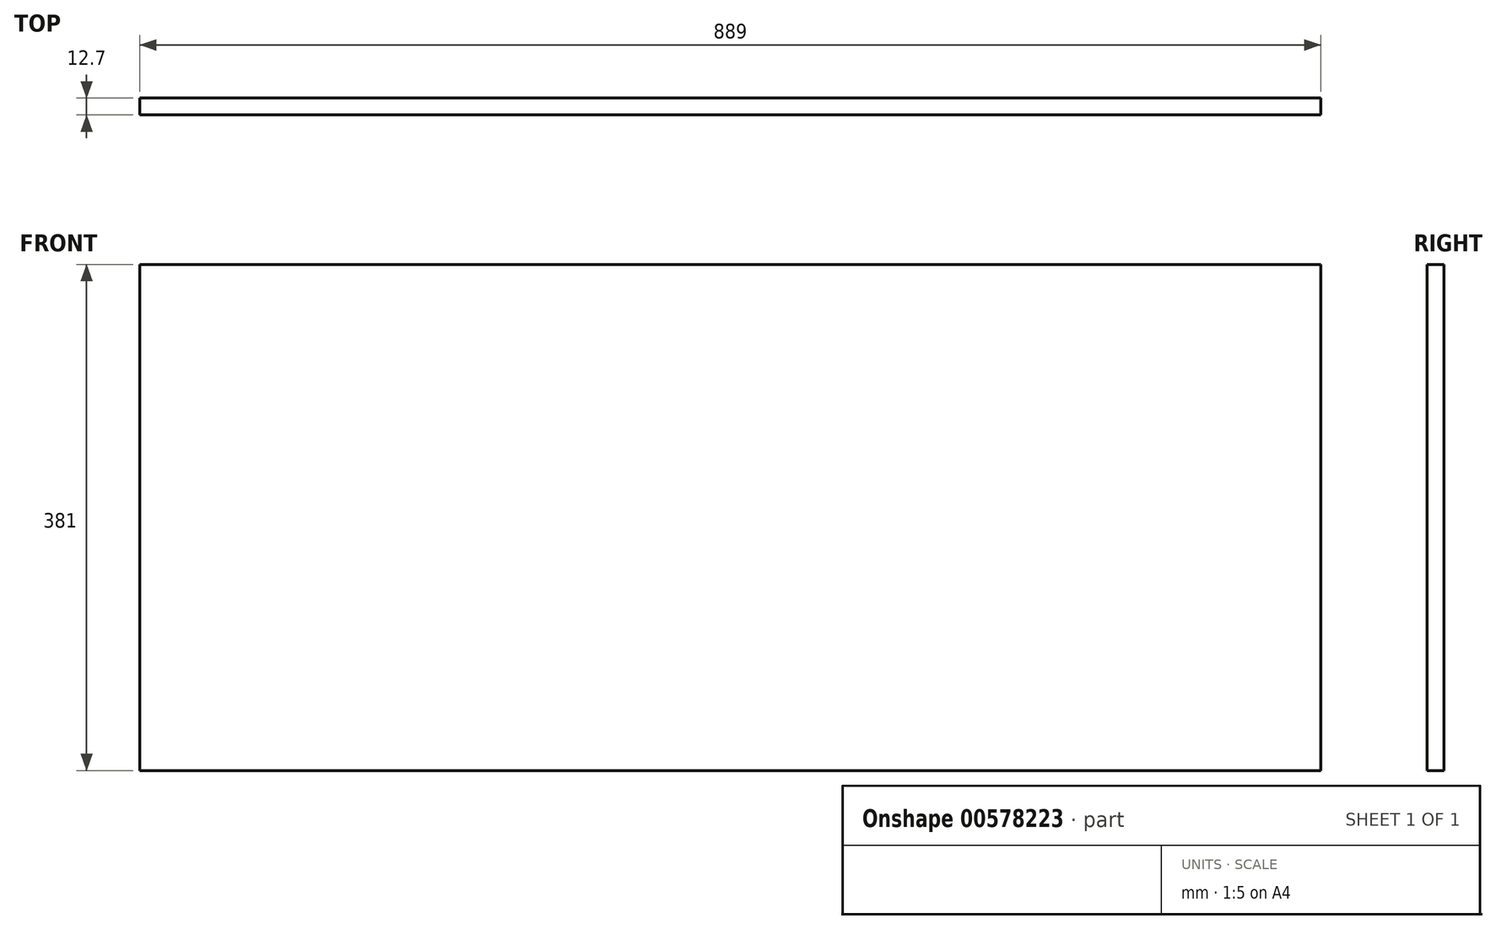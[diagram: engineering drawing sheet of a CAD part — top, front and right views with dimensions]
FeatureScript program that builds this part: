
annotation { "Feature Type Name" : "Feature", "Feature Type Description" : "" }
export const myFeature = defineFeature(function(context is Context, id is Id, definition is map)
    precondition{}
    {
        {
            var Q0;
            Q0=qCreatedBy(makeId("Front.planeOp"),FACE);
            var sketch = newSketch(context, id + "F0", { "sketchPlane" : qUnion([Q0])});
            skLineSegment(sketch, "E0.bottom", {"start": v(-416.26, 231.01) * mm, "end": v(-403.56, 231.01) * mm});
            skLineSegment(sketch, "E0.top", {"start": v(-416.26, -149.99) * mm, "end": v(-403.56, -149.99) * mm});
            skLineSegment(sketch, "E0.left", {"start": v(-416.26, 231.01) * mm, "end": v(-416.26, -149.99) * mm});
            skLineSegment(sketch, "E0.right", {"start": v(472.74, 231.01) * mm, "end": v(472.74, -149.99) * mm});
            skLineSegment(sketch, "E1", {"start": v(-403.56, -149.99) * mm, "end": v(460.04, -149.99) * mm});
            skLineSegment(sketch, "E2", {"start": v(460.04, -149.99) * mm, "end": v(472.74, -149.99) * mm});
            skLineSegment(sketch, "E3", {"start": v(460.04, 231.01) * mm, "end": v(472.74, 231.01) * mm});
            skLineSegment(sketch, "E4", {"start": v(-403.56, 231.01) * mm, "end": v(460.04, 231.01) * mm});
            skLineSegment(sketch, "E5", {"start": v(-403.56, 231.01) * mm, "end": v(-403.56, -149.99) * mm});
            skLineSegment(sketch, "E6", {"start": v(460.04, 231.01) * mm, "end": v(460.04, -149.99) * mm});
            skSolve(sketch);
        }
        {
            var Q0;
            Q0 = qSketchRegion(id + "F0", true);
            extrude(context, id + "F1", {"entities" : qUnion([Q0]), "depth" : 12.7 * mm, "offsetDistance" : 25.4 * mm});
        }
    });
